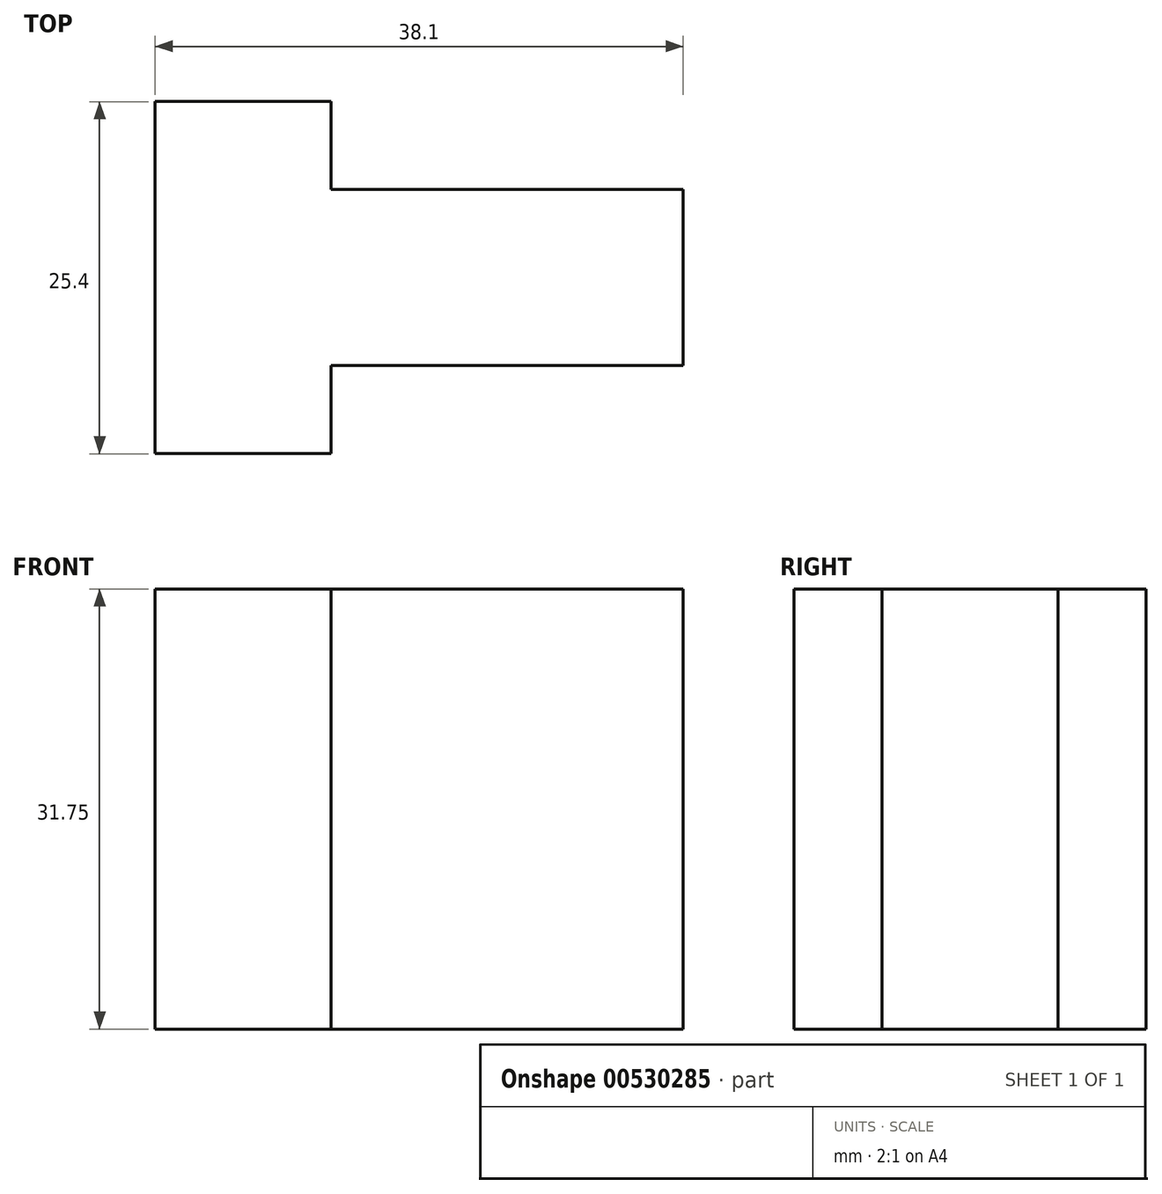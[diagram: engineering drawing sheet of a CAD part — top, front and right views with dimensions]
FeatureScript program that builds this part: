
annotation { "Feature Type Name" : "Feature", "Feature Type Description" : "" }
export const myFeature = defineFeature(function(context is Context, id is Id, definition is map)
    precondition{}
    {
        {
            var Q0;
            Q0=qCreatedBy(makeId("Top.planeOp"),FACE);
            var sketch = newSketch(context, id + "F0", { "sketchPlane" : qUnion([Q0])});
            skLineSegment(sketch, "E0", {"start": v(-20.75, 15.21) * mm, "end": v(-20.75, -10.19) * mm});
            skLineSegment(sketch, "E1", {"start": v(-20.75, -10.19) * mm, "end": v(-8.05, -10.19) * mm});
            skLineSegment(sketch, "E2", {"start": v(-8.05, -10.19) * mm, "end": v(-8.05, -3.84) * mm});
            skLineSegment(sketch, "E3", {"start": v(-8.05, -3.84) * mm, "end": v(17.35, -3.84) * mm});
            skLineSegment(sketch, "E4", {"start": v(-20.75, 15.21) * mm, "end": v(-8.05, 15.21) * mm});
            skLineSegment(sketch, "E5", {"start": v(-8.05, 15.21) * mm, "end": v(-8.05, 8.86) * mm});
            skLineSegment(sketch, "E6", {"start": v(-8.05, 8.86) * mm, "end": v(17.35, 8.86) * mm});
            skLineSegment(sketch, "E7", {"start": v(17.35, 8.86) * mm, "end": v(17.35, -3.84) * mm});
            skSolve(sketch);
        }
        {
            var Q0;
            Q0=makeQuery(id+"F0.imprint","IMPRINT",FACE,{"disambiguationData":[TD([[makeQuery(id+"F0.imprint","IMPRINT",EDGE,{"derivedFrom":sQuery(id+"F0.wireOp",EDGE,"E0")}),1.0]])]});
            extrude(context, id + "F1", {"entities" : qUnion([Q0]), "depth" : 31.75 * mm, "offsetDistance" : 25.4 * mm});
        }
    });
